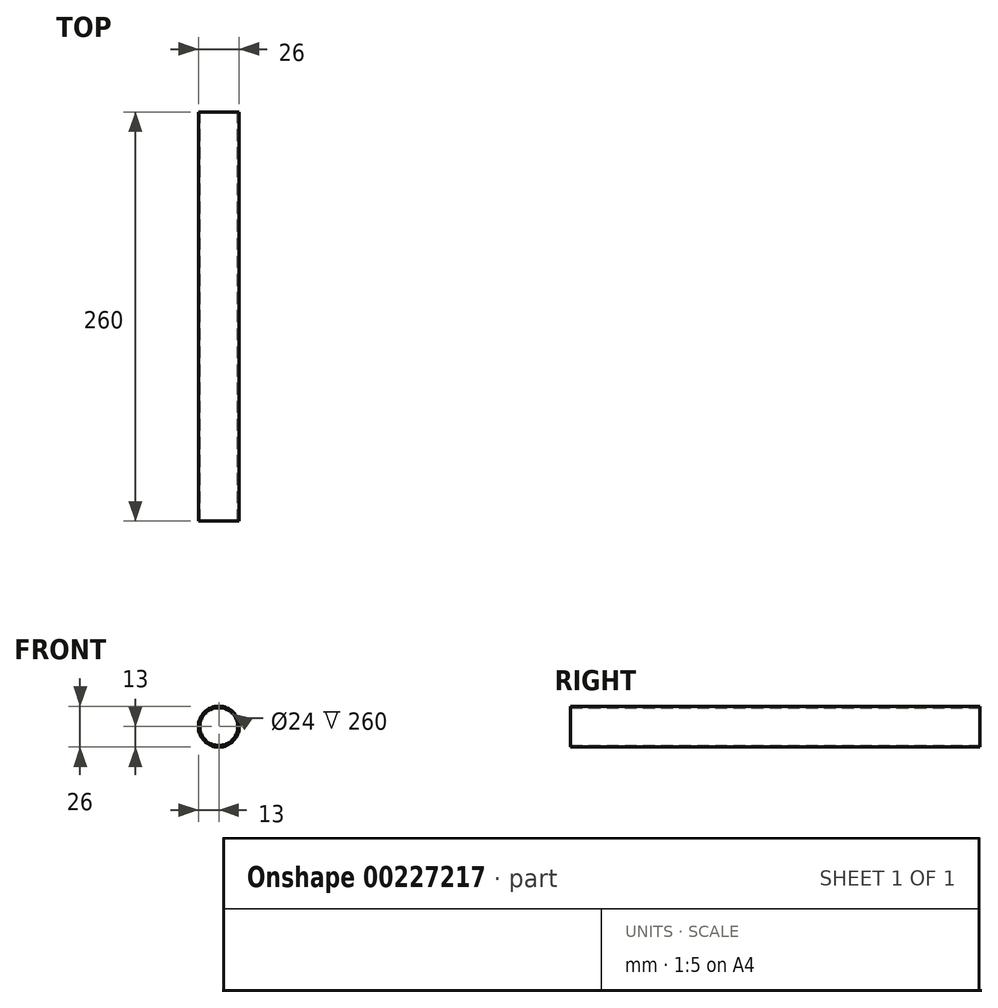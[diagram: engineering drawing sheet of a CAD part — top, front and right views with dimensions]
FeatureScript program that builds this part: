
annotation { "Feature Type Name" : "Feature", "Feature Type Description" : "" }
export const myFeature = defineFeature(function(context is Context, id is Id, definition is map)
    precondition{}
    {
        {
            var Q0;
            Q0=qCreatedBy(makeId("Front.planeOp"),FACE);
            var sketch = newSketch(context, id + "F0", { "sketchPlane" : qUnion([Q0])});
            skCircle(sketch, "E0", {"center": v(0, 0) * mm, "radius": 13 * mm});
            skCircle(sketch, "E1", {"center": v(0, 0) * mm, "radius": 12 * mm});
            skSolve(sketch);
        }
        {
            var Q0;
            Q0 = qSketchRegion(id + "F0", true);
            extrude(context, id + "F1", {"entities" : qUnion([Q0]), "endBound" : BoundingType.SYMMETRIC, "depth" : 260 * mm});
        }
    });
